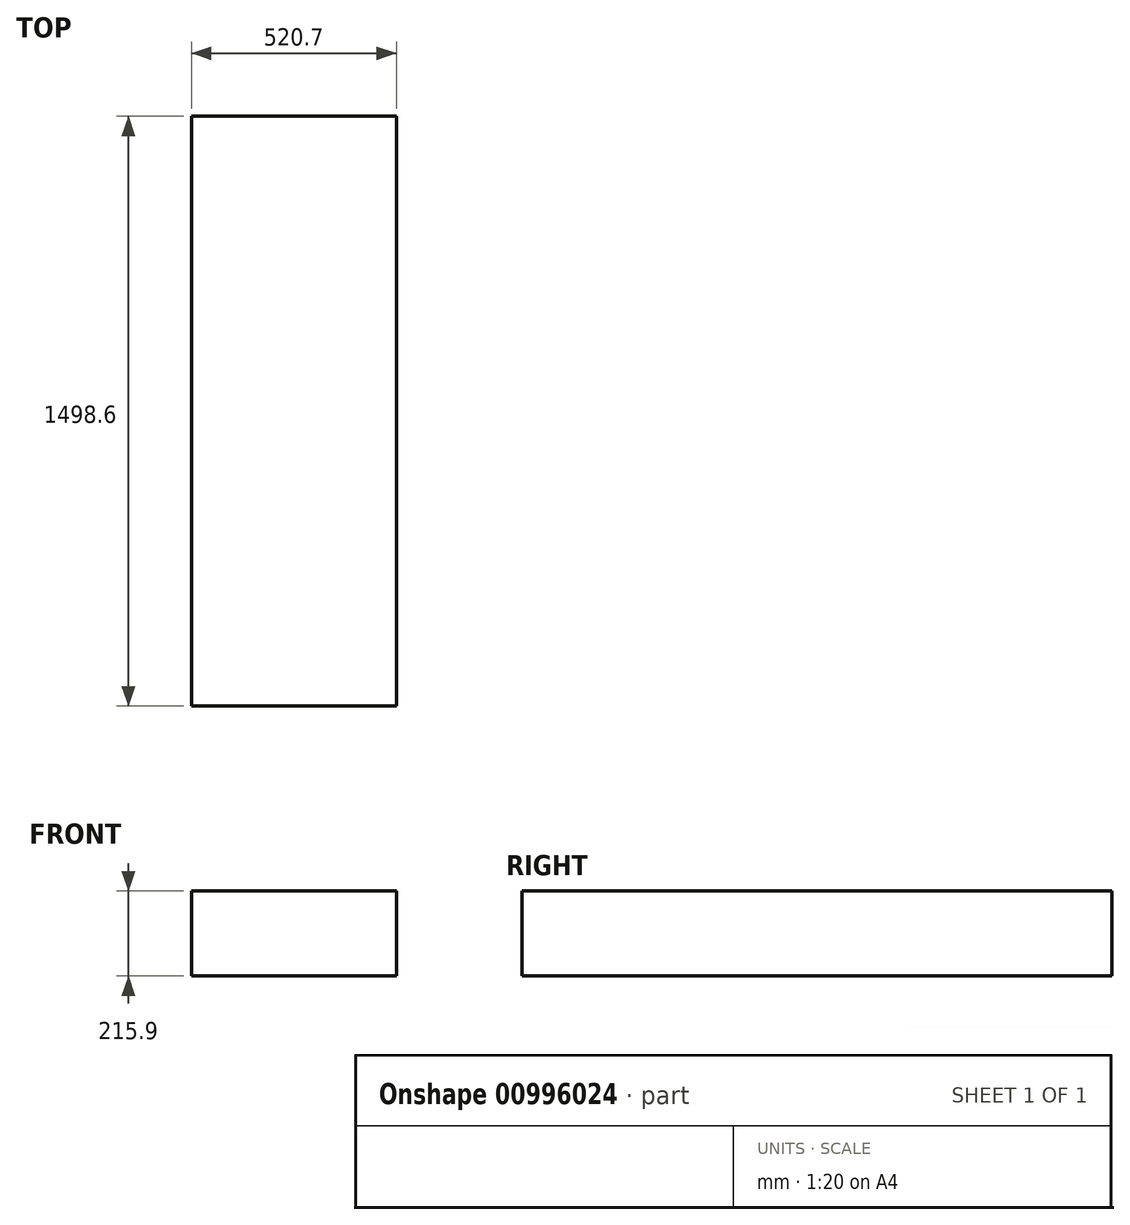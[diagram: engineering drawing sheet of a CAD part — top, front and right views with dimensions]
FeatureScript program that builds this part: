
annotation { "Feature Type Name" : "Feature", "Feature Type Description" : "" }
export const myFeature = defineFeature(function(context is Context, id is Id, definition is map)
    precondition{}
    {
        {
            var Q0;
            Q0=qCreatedBy(makeId("Top.planeOp"),FACE);
            var sketch = newSketch(context, id + "F0", { "sketchPlane" : qUnion([Q0])});
            skLineSegment(sketch, "E0.bottom", {"start": v(0, 0) * mm, "end": v(520.7, 0) * mm});
            skLineSegment(sketch, "E0.top", {"start": v(0, 1498.6) * mm, "end": v(520.7, 1498.6) * mm});
            skLineSegment(sketch, "E0.left", {"start": v(0, 0) * mm, "end": v(0, 1498.6) * mm});
            skLineSegment(sketch, "E0.right", {"start": v(520.7, 0) * mm, "end": v(520.7, 1498.6) * mm});
            skSolve(sketch);
        }
        {
            var Q0;
            Q0=makeQuery(id+"F0.imprint","IMPRINT",FACE,{"disambiguationData":[TD([[makeQuery(id+"F0.imprint","IMPRINT",EDGE,{"derivedFrom":sQuery(id+"F0.wireOp",EDGE,"E0.bottom")}),1.0]])]});
            extrude(context, id + "F1", {"entities" : qUnion([Q0]), "depth" : 215.9 * mm, "offsetDistance" : 25.4 * mm});
        }
    });
